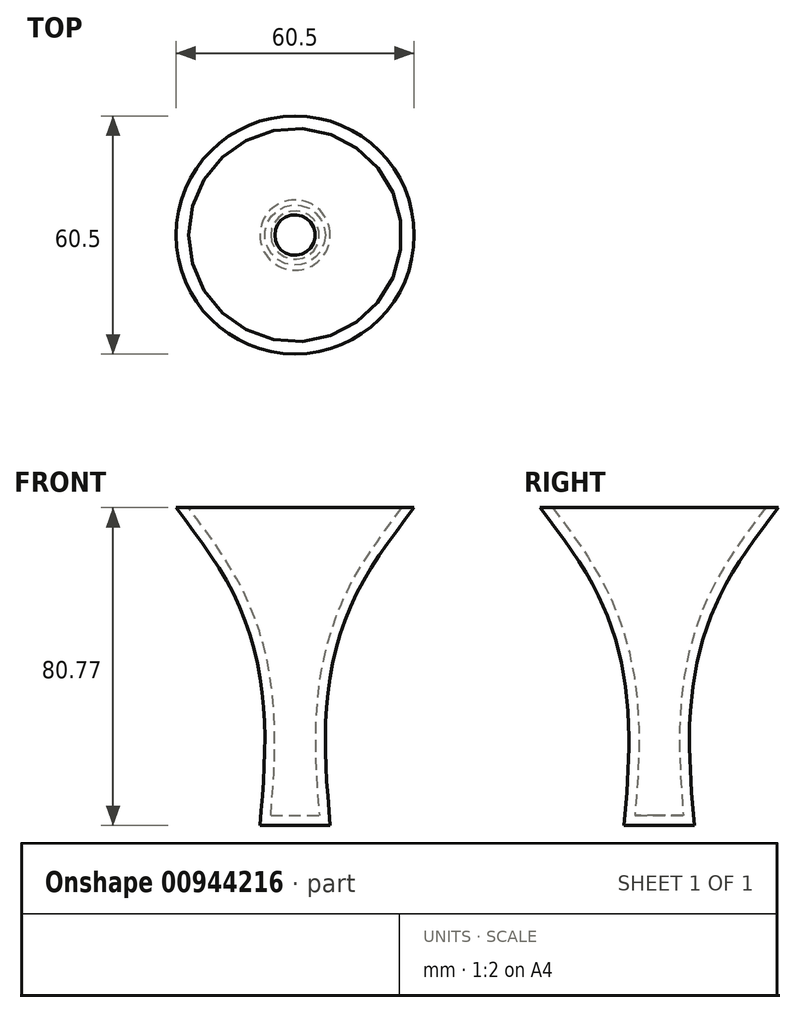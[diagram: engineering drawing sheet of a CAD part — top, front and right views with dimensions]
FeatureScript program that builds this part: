
annotation { "Feature Type Name" : "Feature", "Feature Type Description" : "" }
export const myFeature = defineFeature(function(context is Context, id is Id, definition is map)
    precondition{}
    {
        {
            var Q0;
            Q0=qCreatedBy(makeId("Top.planeOp"),FACE);
            var sketch = newSketch(context, id + "F0", { "sketchPlane" : qUnion([Q0])});
            skCircle(sketch, "E0", {"center": v(0, 0) * mm, "radius": 8.93 * mm});
            skSolve(sketch);
        }
        {
            var Q0;
            Q0=qCreatedBy(makeId("Top.planeOp"),FACE);
            cPlane(context, id + "F1", {"entities" : qUnion([Q0]), "cplaneType" : CPlaneType.OFFSET, "offset" : 80.77 * mm, "width" : 152.4 * mm, "height" : 152.4 * mm});
        }
        {
            var Q0;
            Q0=qCreatedBy(id+"F1.planeOp",FACE);
            var sketch = newSketch(context, id + "F2", { "sketchPlane" : qUnion([Q0])});
            skCircle(sketch, "E1", {"center": v(0, 0) * mm, "radius": 30.25 * mm});
            skSolve(sketch);
        }
        {
            var Q0;
            Q0=qCreatedBy(makeId("Top.planeOp"),FACE);
            cPlane(context, id + "F3", {"entities" : qUnion([Q0]), "cplaneType" : CPlaneType.OFFSET, "offset" : 30.48 * mm, "width" : 152.4 * mm, "height" : 152.4 * mm});
        }
        {
            var Q0;
            Q0=qCreatedBy(makeId("Top.planeOp"),FACE);
            cPlane(context, id + "F4", {"entities" : qUnion([Q0]), "cplaneType" : CPlaneType.OFFSET, "offset" : 56.13 * mm, "width" : 152.4 * mm, "height" : 152.4 * mm});
        }
        {
            var Q0;
            Q0=qCreatedBy(id+"F4.planeOp",FACE);
            var sketch = newSketch(context, id + "F5", { "sketchPlane" : qUnion([Q0])});
            skCircle(sketch, "E2", {"center": v(0, 0) * mm, "radius": 14.35 * mm});
            skSolve(sketch);
        }
        {
            var Q0;
            Q0=qCreatedBy(id+"F3.planeOp",FACE);
            var sketch = newSketch(context, id + "F6", { "sketchPlane" : qUnion([Q0])});
            skCircle(sketch, "E3", {"center": v(0, 0) * mm, "radius": 8.02 * mm});
            skSolve(sketch);
        }
        {
            var Q0;
            Q0=makeQuery(id+"F0.imprint","IMPRINT",FACE,{"disambiguationData":[TD([[makeQuery(id+"F0.imprint","IMPRINT",EDGE,{"derivedFrom":sQuery(id+"F0.wireOp",EDGE,"E0")}),1.0]])]});
            var Q1;
            Q1=makeQuery(id+"F6.imprint","IMPRINT",FACE,{"disambiguationData":[TD([[makeQuery(id+"F6.imprint","IMPRINT",EDGE,{"derivedFrom":sQuery(id+"F6.wireOp",EDGE,"E3")}),1.0]])]});
            var Q2;
            Q2=makeQuery(id+"F5.imprint","IMPRINT",FACE,{"disambiguationData":[TD([[makeQuery(id+"F5.imprint","IMPRINT",EDGE,{"derivedFrom":sQuery(id+"F5.wireOp",EDGE,"E2")}),1.0]])]});
            var Q3;
            Q3=makeQuery(id+"F2.imprint","IMPRINT",FACE,{"disambiguationData":[TD([[makeQuery(id+"F2.imprint","IMPRINT",EDGE,{"derivedFrom":sQuery(id+"F2.wireOp",EDGE,"E1")}),1.0]])]});
            loft(context, id + "F7", {"sheetProfilesArray" : [{ "sheetProfileEntities" : qUnion([Q0]) }, { "sheetProfileEntities" : qUnion([Q1]) }, { "sheetProfileEntities" : qUnion([Q2]) }, { "sheetProfileEntities" : qUnion([Q3]) }]});
        }
        {
            var Q0;
            Q0=makeQuery(id+"F7.opLoft","CAP_FACE",FACE,{"disambiguationData":[OSD([makeQuery(id+"F2.imprint","IMPRINT",FACE,{"disambiguationData":[TD([[makeQuery(id+"F2.imprint","IMPRINT",EDGE,{"derivedFrom":sQuery(id+"F2.wireOp",EDGE,"E1")}),1.0]])]})])],"isStart":true});
            shell(context, id + "F8", {"entities" : qUnion([Q0]), "thickness" : 2.54 * mm});
        }
    });
